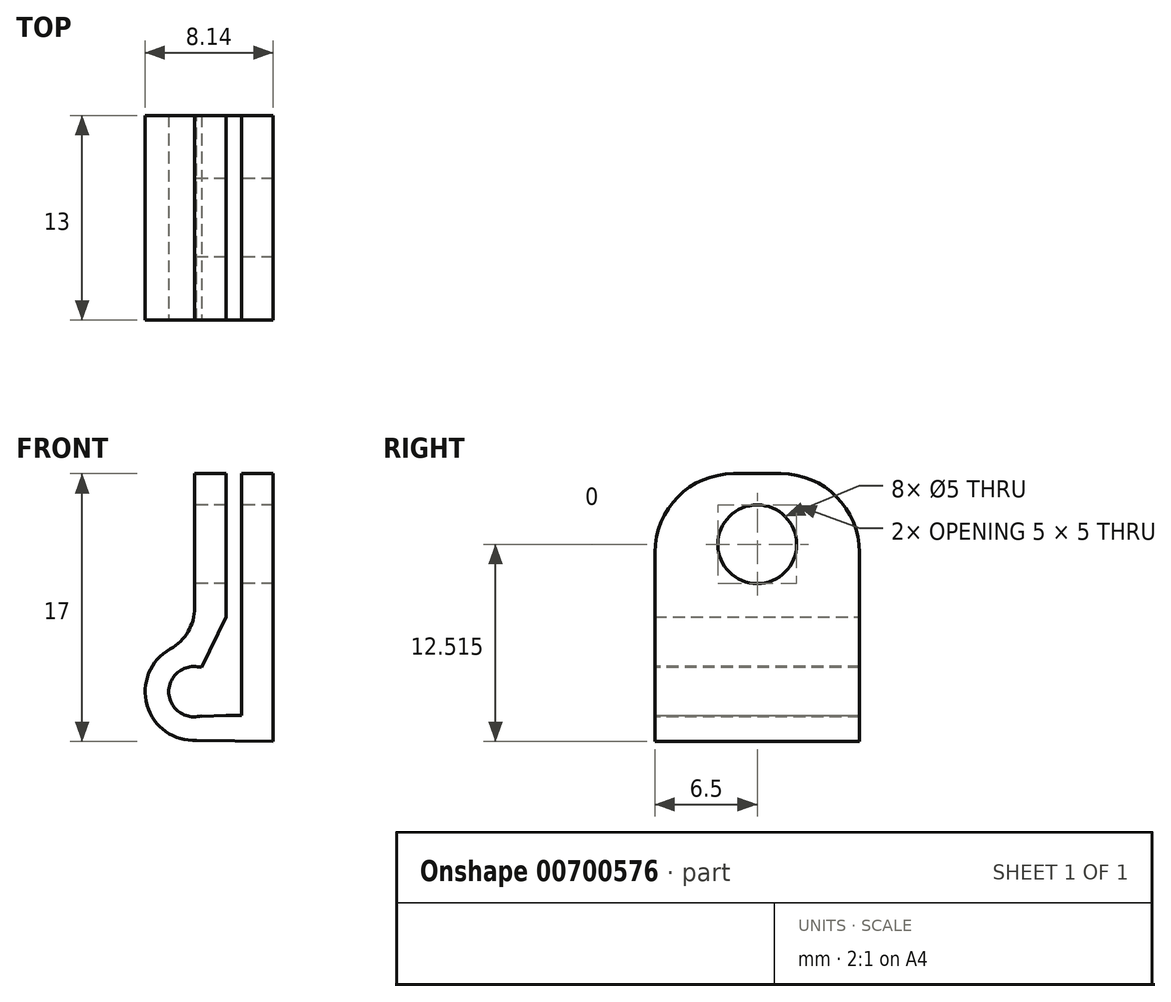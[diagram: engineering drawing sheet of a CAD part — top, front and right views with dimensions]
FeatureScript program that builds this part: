
annotation { "Feature Type Name" : "Feature", "Feature Type Description" : "" }
export const myFeature = defineFeature(function(context is Context, id is Id, definition is map)
    precondition{}
    {
        {
            var Q0;
            Q0=qCreatedBy(makeId("Front.planeOp"),FACE);
            var sketch = newSketch(context, id + "F0", { "sketchPlane" : qUnion([Q0])});
            skLineSegment(sketch, "E0", {"start": v(0, 0) * mm, "end": v(0, 17) * mm});
            skArc(sketch, "E1", {"start": v(-5, 6.26) * mm, "mid": v(-8.14, 3.09) * mm, "end": v(-4.86, 0.06) * mm});
            skLineSegment(sketch, "E2", {"start": v(0, 17) * mm, "end": v(-2, 17) * mm});
            skLineSegment(sketch, "E3", {"start": v(-5, 17) * mm, "end": v(-5, 6.26) * mm});
            skLineSegment(sketch, "E4", {"start": v(0, 0) * mm, "end": v(-4.86, 0.06) * mm});
            skLineSegment(sketch, "E5", {"start": v(-3, 17) * mm, "end": v(-3, 1.65) * mm});
            skLineSegment(sketch, "E6", {"start": v(-3, 1.65) * mm, "end": v(-2, 1.65) * mm});
            skLineSegment(sketch, "E7", {"start": v(-2, 1.65) * mm, "end": v(-2, 17) * mm});
            skLineSegment(sketch, "E8.trimOffspring", {"start": v(-3, 17) * mm, "end": v(-5, 17) * mm});
            skSolve(sketch);
        }
        {
            var Q0;
            Q0 = qSketchRegion(id + "F0", true);
            extrude(context, id + "F1", {"entities" : qUnion([Q0]), "depth" : 13 * mm, "offsetDistance" : 25 * mm});
        }
        {
            var Q0;
            Q0=makeQuery(id+"F1.opExtrude","CAP_FACE",FACE,{"disambiguationData":[OSD([sQuery(id+"F0.wireOp",EDGE,"E0"),sQuery(id+"F0.wireOp",EDGE,"E1"),sQuery(id+"F0.wireOp",EDGE,"E2"),sQuery(id+"F0.wireOp",EDGE,"E3"),sQuery(id+"F0.wireOp",EDGE,"E4"),sQuery(id+"F0.wireOp",EDGE,"E5"),sQuery(id+"F0.wireOp",EDGE,"E6"),sQuery(id+"F0.wireOp",EDGE,"E7"),sQuery(id+"F0.wireOp",EDGE,"E8.trimOffspring")])],"isStart":false});
            var sketch = newSketch(context, id + "F2", { "sketchPlane" : qUnion([Q0])});
            skArc(sketch, "E9.0", {"start": v(-5, 6.26) * mm, "mid": v(-8.14, 3.09) * mm, "end": v(-4.86, 0.06) * mm});
            skCircle(sketch, "E10", {"center": v(-5.04, 3.16) * mm, "radius": 1.6 * mm});
            skSolve(sketch);
        }
        {
            var Q0;
            Q0 = qSketchRegion(id + "F2", true);
            extrude(context, id + "F3", {"entities" : qUnion([Q0]), "operationType" : NewBodyOperationType.REMOVE, "oppositeDirection" : true, "depth" : 25 * mm, "offsetDistance" : 25 * mm});
        }
        {
            var Q0;
            Q0=makeQuery(id+"F1.opExtrude","CAP_FACE",FACE,{"disambiguationData":[OSD([sQuery(id+"F0.wireOp",EDGE,"E0"),sQuery(id+"F0.wireOp",EDGE,"E1"),sQuery(id+"F0.wireOp",EDGE,"E2"),sQuery(id+"F0.wireOp",EDGE,"E3"),sQuery(id+"F0.wireOp",EDGE,"E4"),sQuery(id+"F0.wireOp",EDGE,"E5"),sQuery(id+"F0.wireOp",EDGE,"E6"),sQuery(id+"F0.wireOp",EDGE,"E7"),sQuery(id+"F0.wireOp",EDGE,"E8.trimOffspring")])],"isStart":false});
            var sketch = newSketch(context, id + "F4", { "sketchPlane" : qUnion([Q0])});
            skLineSegment(sketch, "E11", {"start": v(-4.55, 4.68) * mm, "end": v(-2.6, 8.75) * mm});
            skLineSegment(sketch, "E12", {"start": v(-2.6, 8.75) * mm, "end": v(-2.6, 3.03) * mm});
            skLineSegment(sketch, "E13", {"start": v(-2.6, 3.03) * mm, "end": v(-4.6, 3.03) * mm});
            skLineSegment(sketch, "E14", {"start": v(-4.6, 3.03) * mm, "end": v(-4.55, 4.68) * mm});
            skLineSegment(sketch, "E15", {"start": v(-3, 1.65) * mm, "end": v(-4.55, 1.58) * mm});
            skLineSegment(sketch, "E16", {"start": v(-4.55, 1.58) * mm, "end": v(-4.6, 3.03) * mm});
            skLineSegment(sketch, "E17", {"start": v(-2.6, 3.03) * mm, "end": v(-3, 1.65) * mm});
            skSolve(sketch);
        }
        {
            var Q0;
            Q0 = qSketchRegion(id + "F4", true);
            extrude(context, id + "F5", {"entities" : qUnion([Q0]), "operationType" : NewBodyOperationType.REMOVE, "oppositeDirection" : true, "depth" : 25 * mm, "offsetDistance" : 25 * mm});
        }
        {
            var Q0;
            Q0=makeQuery(id+"F1.opExtrude","SWEPT_EDGE",EDGE,{"disambiguationData":[OSD([sQuery(id+"F0.wireOp",EDGE,"E1"),sQuery(id+"F0.wireOp",EDGE,"E3")])]});
            fillet(context, id + "F6", {"entities" : qUnion([Q0]), "radius" : 3 * mm, "tangentPropagation" : true, "allowEdgeOverflow" : false});
        }
        {
            var Q0;
            Q0=makeQuery(id+"F1.opExtrude","CAP_EDGE",EDGE,{"disambiguationData":[OSD([sQuery(id+"F0.wireOp",EDGE,"E8.trimOffspring")])],"isStart":true});
            var Q1;
            Q1=makeQuery(id+"F1.opExtrude","CAP_EDGE",EDGE,{"disambiguationData":[OSD([sQuery(id+"F0.wireOp",EDGE,"E2")])],"isStart":true});
            var Q2;
            Q2=makeQuery(id+"F1.opExtrude","CAP_EDGE",EDGE,{"disambiguationData":[OSD([sQuery(id+"F0.wireOp",EDGE,"E8.trimOffspring")])],"isStart":false});
            var Q3;
            Q3=makeQuery(id+"F1.opExtrude","CAP_EDGE",EDGE,{"disambiguationData":[OSD([sQuery(id+"F0.wireOp",EDGE,"E2")])],"isStart":false});
            fillet(context, id + "F7", {"entities" : qUnion([Q0, Q1, Q2, Q3]), "radius" : 5 * mm, "tangentPropagation" : true, "allowEdgeOverflow" : false});
        }
        {
            var Q0;
            Q0=makeQuery(id+"F1.opExtrude","SWEPT_FACE",FACE,{"disambiguationData":[OSD([sQuery(id+"F0.wireOp",EDGE,"E3")])]});
            var sketch = newSketch(context, id + "F8", { "sketchPlane" : qUnion([Q0])});
            skLineSegment(sketch, "E18.0", {"start": v(8, 17) * mm, "end": v(5, 17) * mm});
            skLineSegment(sketch, "E19.0", {"start": v(0, 12) * mm, "end": v(0, 8.49) * mm});
            skLineSegment(sketch, "E20.0", {"start": v(13, 12) * mm, "end": v(13, 8.49) * mm});
            skCircle(sketch, "E21", {"center": v(6.5, 12.52) * mm, "radius": 2.5 * mm});
            skPoint(sketch, "E21.centerSnap0", {"position": v(6.5, 17) * mm});
            skSolve(sketch);
        }
        {
            var Q0;
            Q0 = qSketchRegion(id + "F8", true);
            extrude(context, id + "F9", {"entities" : qUnion([Q0]), "operationType" : NewBodyOperationType.REMOVE, "oppositeDirection" : true, "depth" : 25 * mm, "offsetDistance" : 25 * mm});
        }
    });
